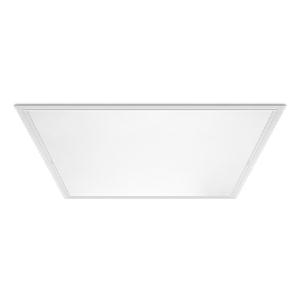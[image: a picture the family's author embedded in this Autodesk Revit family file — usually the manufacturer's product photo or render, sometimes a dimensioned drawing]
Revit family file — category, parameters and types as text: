
# Revit family: 3f_filippi_-_l_340_luce_diffusa_vs_ip65v_3f_filippi_-_23929_-_l_340_29w-940_ep_vs_ip65v_596x596
name_source: partatom
category: Lighting Fixtures
units: mm (PartAtom-declared; Revit-internal decimal feet)

## family parameters
Cut with Voids When Loaded = No
Host = Face
Light Source = No
Part Type = Normal
Room Calculation Point = No
Round Connector Dimension = Use Diameter
Shared = No

## types (1)
- 3F Filippi - L 340 Luce Diffusa VS IP65V (1 x LED, 3155 lm, 36 W, 4000 K)
    Apparent Load = 36 VA
    Approval mark = ENEC
    CIE Flux Codes = 61 89 98 100 100
    Color Rendering = 90
    Color Temperature = 4000 K
    Control Gear = Electronic ballast
    Default Elevation = 1800 mm
    Description = ILLUMINOTECHNICAL
Luminous efficiency 100% (DLOR 100%, ULOR 0%).
Initial luminous flux of the luminaire 3155 lm.
Emergency luminaire luminous flux BLF 12%.
Direct symmetric distribution.
Installation Interdistance Transv.D = 1.17 x hu - Long.D = 1.14 x hu.
Average luminance <3000 cd/m² for radial angles >65°.
Tabular UGR (CIE 117 - 4H-8H; S=0.25H; 70/50/20): RUG 17.2 - 17.
Beam angle: 91° - 88°.
Luminous efficacy 88 lm/W.
Lifetime (L93/B10): 30000 h. (tq+25°C)
Lifetime (L90/B10): 50000 h. (tq+25°C)
Lifetime (L85/B10): 80000 h. (tq+25°C)
Lifetime (L80/B10): 100000 h. (tq+25°C)
Sudden decreased luminous flux after 50000 hours: 0% (C0).
Photobiological safety in compliance with IEC/TR 62778: RG0 risk exempt, (IEC 62471).
In compliance with IEC/EN 62722-2-1 - IEC/EN 62717 standards.

SOURCE
Squared LED module 29W/940.
Energy efficiency class (UE 2019/2020 - UE 2019/2015): D.
CIE 13.3 Colour rendering index: CRI >90 (R9 >50%).
IES TM-30 Fidelity Index: Rf = 92 Rg = 101.
CCT nominal colour temperature 4000 K.
Colour initial tolerance (MacAdam): SDCM 3.

MECHANICAL
Housing in hot-galvanised steel, painted in white polyester.
Perimetral frame in white polycarbonate.
VS moulded glass, anti-glare, tempered, non-combustible, thickness 4 mm.
Luminaire with limited surface temperature. - D - (EN 60598-2-24)
Dimensions: 596x596 mm, height 80 mm. Weight 7.2 kg.
IP65 protection degree for exposed part, IP40 for recessed part.
Mechanical strength to impacts IK08 (5 joule).
Glow-wire test resistance 960°C.

ELECTRICAL
Wiring on a separate unit.
Halogen Free electronic wiring 230V-50/60Hz, power factor 0.90, THD <25%, constant output current, SELV, class II, 1 driver.
Power of the luminaire 36 W.
CE - IEC 60598-1 - EN 60598-1.
EP maintained emergency wiring on board, 1h duration, 24h recharge; compliant with EN 60598-2-22, excluding high risk areas.
SAFE FLICKER: PstLM=<1 and SVM=<0.4 (IEC TR 61547-1 and IEC TR 63158), to ensure a more comfortable and safe light.
Ambient temperature from +5°C to +25°C.
Temperature class T6 max 85°C.
Relative humidity UR: <85%.

INSTALLATION
Lay-on or pull-up recessed fitting using frame and anti-fall safety cable accessories.
All accessories dedicated to this product are available on the Catalog and on our website www.3F-Filippi.com.

APPLICATIONS
In environments requiring protection and simplified cleaning.
Hospitals, pharmaceutical, chemical, aseptic laboratories, sterilised rooms.
Environments: with VDTs, meeting rooms, offices.
Environments: architectural, commercial, staterooms, banks.
Environments where demanding visual tasks are performed and soft diffuse light is required for optimal visual comfort and total shielding of the light source.

WARNING
Luminaire designed for disposal/recycling at end-of-life.
Replaceable (LED only) light source by a professional. Replaceable control gear by a professional.
    Height = 0 mm  [stored 0 ft]
    Lamp = 1 x LED
    Lamp Light Flux = 3155 lm
    Lamp Power = 36 W
    Lamp count = 1
    Length = 596 mm
    Lifetime = 50000 h
    Luminous efficacy = 88 lm/W
    Manufacturer = 3F Filippi
    ModVariant = No
    Model = 3F Filippi - 23929 - L 340 29W-940 EP VS IP65V 596x596
    Mounting Place = Ceiling
    Mounting Type = Recessed
    Number of Poles = 1
    OnlyDefault = Yes
    Power Factor = 1
    Product Name = 3F Filippi - L 340 Luce Diffusa VS IP65V
    Product group = recessed luminaire
    ProductGroupID = 4
    Protection Class = Protection class II
    Protection Degree = IP 40
    RLX_Detail_Level = 1
    RLX_Emergency_Light_Flux = 0 lm
    RLX_Emergency_Type = 0
    RLX_Emergency_Type_DB = No
    RlxData = <blob elided: 153077 chars, md5=da471e14>
    Socket = socket
    Standby Power = 0 W
    System Light Flux = 3155 lm
    System Power = 36 W
    Type Comments = Product without accessories
    Type Image = 3ffilippi_l_340_luce_diffusa_vs.jpg
    URL = http://relux.com
    VarID = ---
    Voltage = 0 V
    Weight = 0.00 kg
    Width = 596 mm

note: [stored X ft] marks values corroborated as IEEE doubles in the binary element streams (Revit-internal decimal feet)

## geometry (parser evidence)
native form markers: Blend x4, Sweep x11
no freeform markers — native parametric forms only
